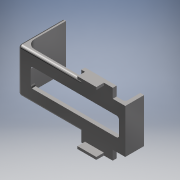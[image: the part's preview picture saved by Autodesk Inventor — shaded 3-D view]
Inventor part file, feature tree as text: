
AUTODESK INVENTOR PART (.ipt)
format: ipt  version: 2018 (Build 220112000, 112)  size: 199,168 bytes
history: native  units: mm
features: extrude x4, fillet x4, sketch x4
ambient origin geometry x8: Origin, YZ Plane, XZ Plane, XY Plane, X Axis, Y Axis, Z Axis, Center Point
bodies: Volumenkörper1 (feature_tree)
feature tree (12):
  extrude  "Extrusion1"  Depth=25.0mm
  extrude  "Extrusion2"  Depth=35.0mm
  fillet  "Rundung1"  Radius=10.0mm
  extrude  "Extrusion3"  Depth=70.0mm
  extrude  "Extrusion4"  Depth=3.0mm TaperAngle=0.0deg
  fillet  "Rundung2"  Radius=3.0mm
  fillet  "Rundung3"  Radius=12.0mm
  fillet  "Rundung4"  Radius=3.0mm
  sketch  "Skizze1"  dims[d0=50.0mm d1=25.0mm]
  sketch  "Skizze2"  dims[d2=7.5mm d4=35.0mm d5=10.0mm]
  sketch  "Skizze3"  dims[d6=15.0mm d8=70.0mm]
  sketch  "Skizze4"  dims[d9=65.0mm d10=3.0mm d11=0.0mm d12=3.0mm d13=12.0mm d14=3.0mm d15=0.0mm d16=2.0mm d17=2.0mm d18=2.0mm d19=46.0mm d20=15.0mm d21=15.0mm d22=0.0mm d23=7.0mm d24=6.0mm d25=0.0mm d26=50.0mm d27=35.0mm d28=7.5mm d29=35.0mm d30=3.0mm d31=0.0mm d32=7.0mm d33=2.0mm d34=2.0mm]
